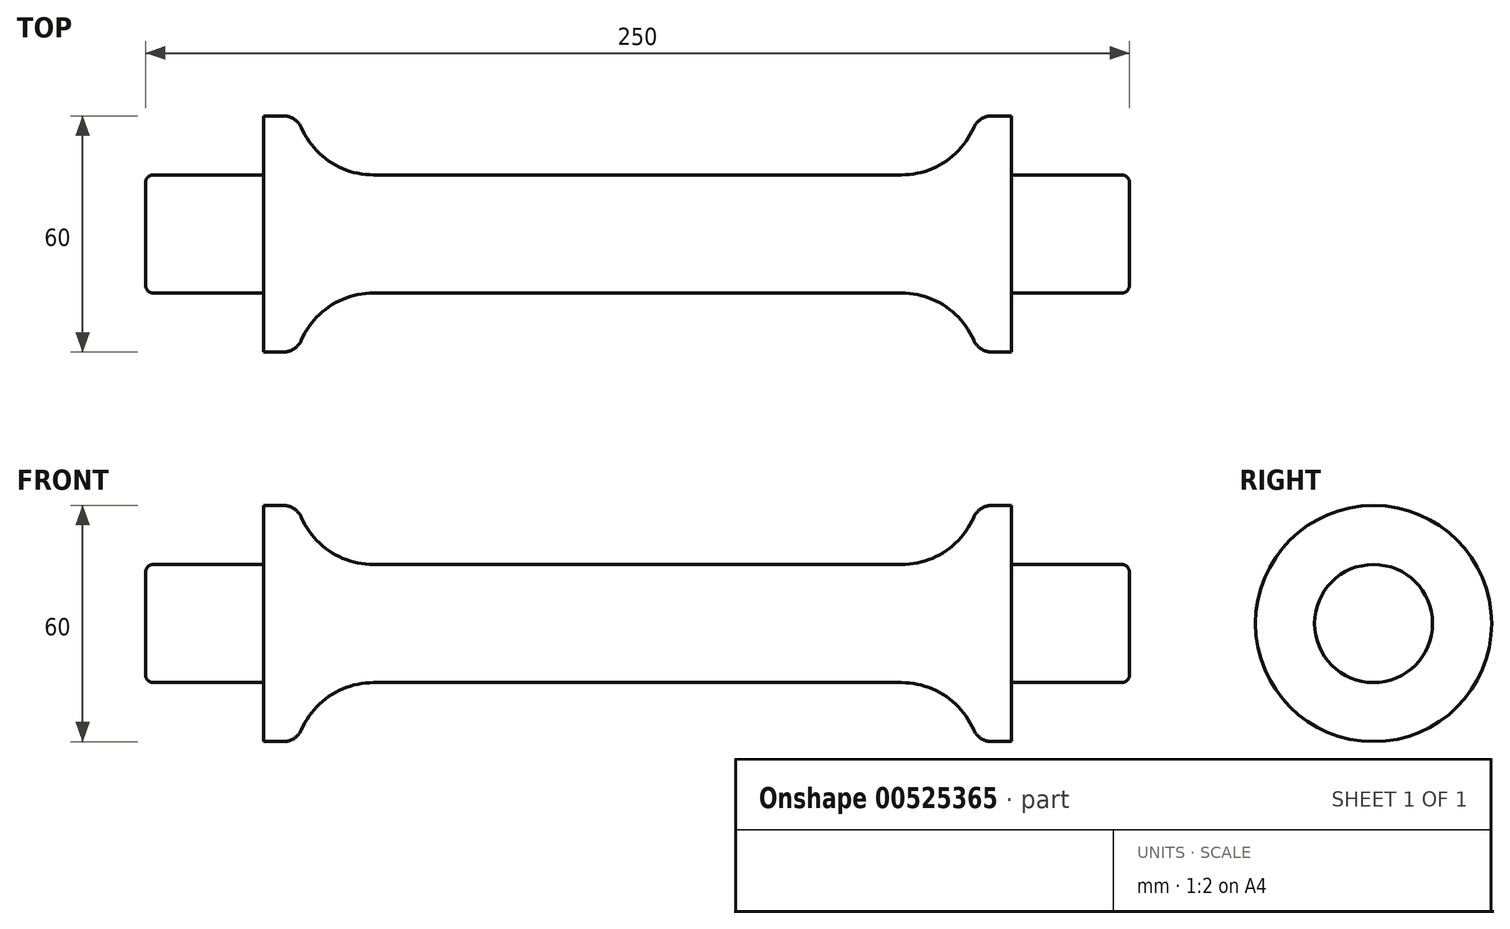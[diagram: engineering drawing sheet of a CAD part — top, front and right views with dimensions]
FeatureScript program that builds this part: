
annotation { "Feature Type Name" : "Feature", "Feature Type Description" : "" }
export const myFeature = defineFeature(function(context is Context, id is Id, definition is map)
    precondition{}
    {
        {
            var Q0;
            Q0=qCreatedBy(makeId("Front.planeOp"),FACE);
            var sketch = newSketch(context, id + "F0", { "sketchPlane" : qUnion([Q0])});
            skLineSegment(sketch, "E0", {"start": v(0, 15.23) * mm, "end": v(67.09, 15.23) * mm});
            skLineSegment(sketch, "E1", {"start": v(87.09, 33.23) * mm, "end": v(87.09, 35.23) * mm});
            skLineSegment(sketch, "E2", {"start": v(90, 30.23) * mm, "end": v(95, 30.23) * mm});
            skLineSegment(sketch, "E3", {"start": v(95, 30.23) * mm, "end": v(95, 15.23) * mm});
            skLineSegment(sketch, "E4", {"start": v(95, 15.23) * mm, "end": v(125, 15.23) * mm});
            skLineSegment(sketch, "E5", {"start": v(125, 15.23) * mm, "end": v(125, 0.23) * mm});
            skLineSegment(sketch, "E6", {"start": v(125, 0.23) * mm, "end": v(0, 0.23) * mm});
            skLineSegment(sketch, "E7", {"start": v(0, 0.23) * mm, "end": v(0, 15.23) * mm});
            skPoint(sketch, "E8.visualSharp", {"position": v(87.09, 15.23) * mm});
            skArc(sketch, "E8.filletArc", {"start": v(67.09, 15.23) * mm, "mid": v(78.04, 18.5) * mm, "end": v(85.42, 27.23) * mm});
            skPoint(sketch, "E9.newPointB", {"position": v(85, 30.23) * mm});
            skArc(sketch, "E9.filletArc", {"start": v(90, 30.23) * mm, "mid": v(87.26, 29.42) * mm, "end": v(85.42, 27.23) * mm});
            skSolve(sketch);
        }
        {
            var Q0;
            Q0=makeQuery(id+"F0.imprint","IMPRINT",FACE,{"disambiguationData":[TD([[makeQuery(id+"F0.imprint","IMPRINT",EDGE,{"derivedFrom":sQuery(id+"F0.wireOp",EDGE,"E0")}),-1.0]])]});
            var Q1;
            Q1=sQuery(id+"F0.wireOp",EDGE,"E6");
            revolve(context, id + "F1", {"entities" : qUnion([Q0]), "axis" : qUnion([Q1]), "revolveType" : RevolveType.FULL});
        }
        {
            var Q0;
            Q0=makeQuery(id+"F1.opRevolve","SWEPT_BODY",BODY,{"disambiguationData":[OSD([sQuery(id+"F0.wireOp",EDGE,"E0"),sQuery(id+"F0.wireOp",EDGE,"E2"),sQuery(id+"F0.wireOp",EDGE,"E3"),sQuery(id+"F0.wireOp",EDGE,"E4"),sQuery(id+"F0.wireOp",EDGE,"E5"),sQuery(id+"F0.wireOp",EDGE,"E6"),sQuery(id+"F0.wireOp",EDGE,"E7"),sQuery(id+"F0.wireOp",EDGE,"E8.filletArc"),sQuery(id+"F0.wireOp",EDGE,"E9.filletArc")])]});
            var Q1;
            Q1=makeQuery(id+"F1.opRevolve","SWEPT_FACE",FACE,{"disambiguationData":[OSD([sQuery(id+"F0.wireOp",EDGE,"E7")])]});
            mirror(context, id + "F2", {"operationType" : NewBodyOperationType.ADD, "entities" : qUnion([Q0]), "mirrorPlane" : qUnion([Q1])});
        }
        {
            var Q0;
            Q0=makeQuery(id+"F2.opPattern","COPY",EDGE,{"derivedFrom":makeQuery(id+"F1.opRevolve","SWEPT_EDGE",EDGE,{"disambiguationData":[OSD([sQuery(id+"F0.wireOp",EDGE,"E4"),sQuery(id+"F0.wireOp",EDGE,"E5")])]}),"instanceName":"1"});
            var Q1;
            Q1=makeQuery(id+"F1.opRevolve","SWEPT_EDGE",EDGE,{"disambiguationData":[OSD([sQuery(id+"F0.wireOp",EDGE,"E4"),sQuery(id+"F0.wireOp",EDGE,"E5")])]});
            fillet(context, id + "F3", {"entities" : qUnion([Q0, Q1]), "radius" : 2 * mm, "tangentPropagation" : true, "allowEdgeOverflow" : false});
        }
    });
